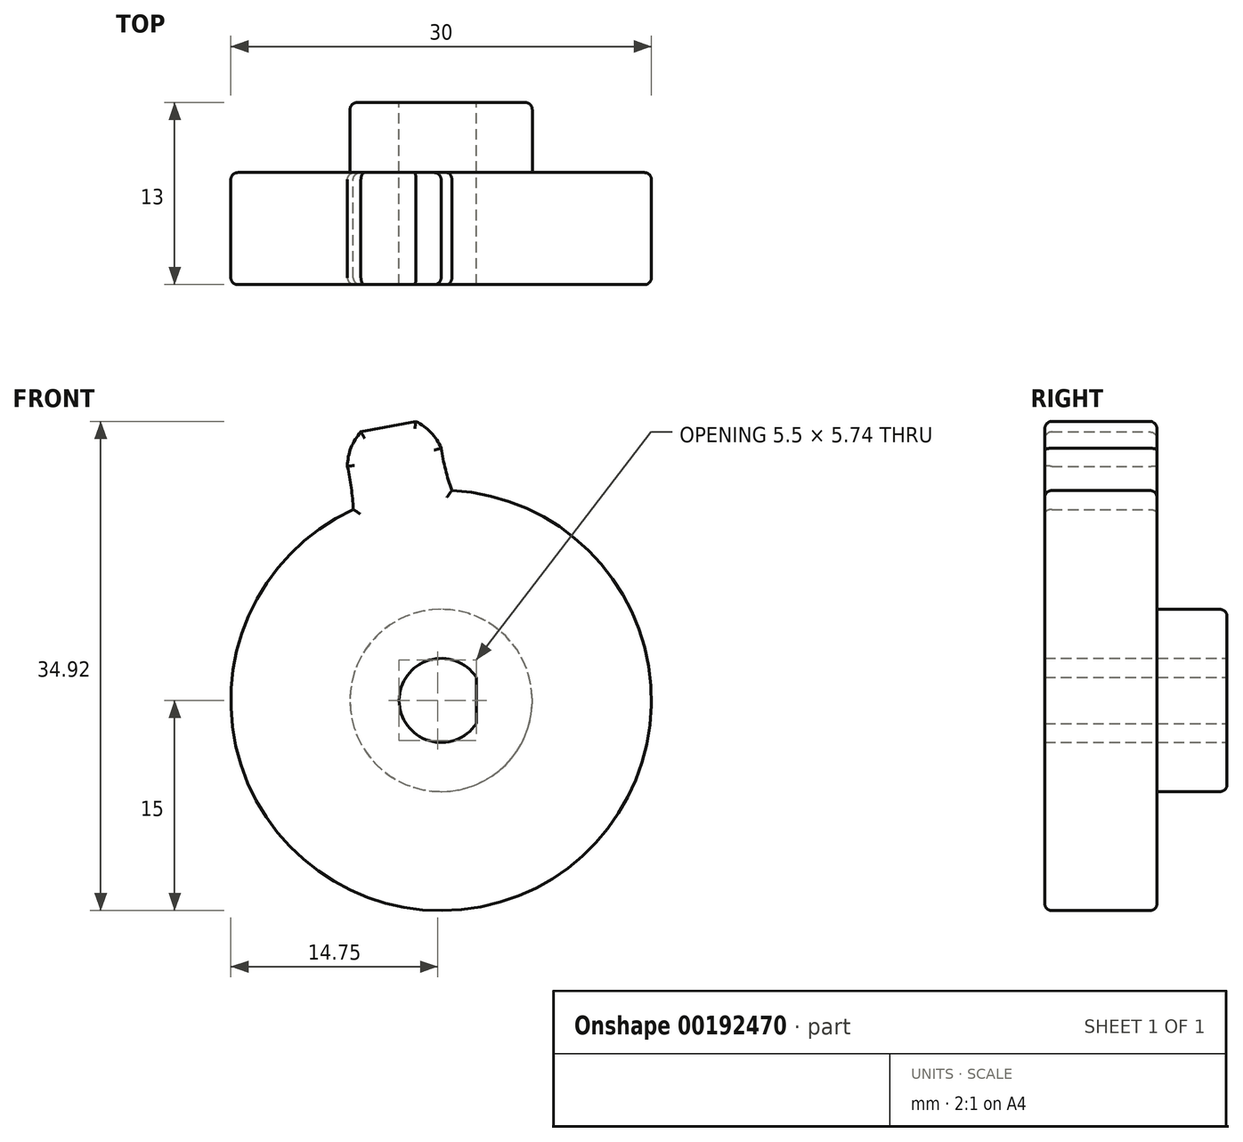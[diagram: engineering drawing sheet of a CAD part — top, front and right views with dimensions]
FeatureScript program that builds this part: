
annotation { "Feature Type Name" : "Feature", "Feature Type Description" : "" }
export const myFeature = defineFeature(function(context is Context, id is Id, definition is map)
    precondition{}
    {
        {
            var Q0;
            Q0=qCreatedBy(makeId("Front.planeOp"),FACE);
            var sketch = newSketch(context, id + "F0", { "sketchPlane" : qUnion([Q0])});
            skCircle(sketch, "E0", {"center": v(0, 0) * mm, "radius": 18 * mm, "construction": true});
            skCircle(sketch, "E1", {"center": v(0, 0) * mm, "radius": 20 * mm, "construction": true});
            skCircle(sketch, "E2", {"center": v(0, 0) * mm, "radius": 15 * mm});
            skLineSegment(sketch, "E3", {"start": v(0, 0) * mm, "end": v(0, 26.07) * mm, "construction": true});
            skLineSegment(sketch, "E4", {"start": v(0, 0) * mm, "end": v(-5, 25.97) * mm, "construction": true});
            skLineSegment(sketch, "E5", {"start": v(0, 18) * mm, "end": v(-27.92, 18) * mm, "construction": true});
            skLineSegment(sketch, "E6", {"start": v(0, 18) * mm, "end": v(-28.83, 7.5) * mm, "construction": true});
            skCircle(sketch, "E7", {"center": v(0, 18) * mm, "radius": 3.75 * mm, "construction": true});
            skCircle(sketch, "E8", {"center": v(0, 0) * mm, "radius": 16.91 * mm, "construction": true});
            skCircle(sketch, "E9", {"center": v(-3.46, 16.56) * mm, "radius": 3.75 * mm, "construction": true});
            skArc(sketch, "E10", {"start": v(0, 18) * mm, "mid": v(-0.72, 19.12) * mm, "end": v(-1.8, 19.92) * mm});
            skArc(sketch, "E11", {"start": v(0, 18) * mm, "mid": v(0.31, 16.47) * mm, "end": v(0.76, 14.98) * mm});
            skArc(sketch, "E12.MirrorCS", {"start": v(-6.68, 16.71) * mm, "mid": v(-6.4, 15.18) * mm, "end": v(-6.27, 13.63) * mm});
            skArc(sketch, "E13.MirrorCS", {"start": v(-6.68, 16.71) * mm, "mid": v(-6.43, 18.03) * mm, "end": v(-5.72, 19.16) * mm});
            skLineSegment(sketch, "E14", {"start": v(-5.72, 19.16) * mm, "end": v(-1.8, 19.92) * mm});
            skArc(sketch, "E15.1.0", {"start": v(-14.14, 11.13) * mm, "mid": v(-14.58, 12.4) * mm, "end": v(-14.54, 13.73) * mm});
            skArc(sketch, "E15.1.1", {"start": v(-14.14, 11.13) * mm, "mid": v(-13.14, 9.94) * mm, "end": v(-12.24, 8.67) * mm});
            skArc(sketch, "E15.1.2", {"start": v(-9, 15.59) * mm, "mid": v(-7.96, 14.42) * mm, "end": v(-6.83, 13.35) * mm});
            skArc(sketch, "E15.1.3", {"start": v(-9, 15.59) * mm, "mid": v(-10.19, 16.2) * mm, "end": v(-11.52, 16.35) * mm});
            skLineSegment(sketch, "E15.1.4", {"start": v(-14.54, 13.73) * mm, "end": v(-11.52, 16.35) * mm});
            skArc(sketch, "E15.2.0", {"start": v(-17.82, 2.57) * mm, "mid": v(-18.83, 3.45) * mm, "end": v(-19.46, 4.62) * mm});
            skArc(sketch, "E15.2.1", {"start": v(-17.82, 2.57) * mm, "mid": v(-16.35, 2.04) * mm, "end": v(-14.94, 1.38) * mm});
            skArc(sketch, "E15.2.2", {"start": v(-15.59, 9) * mm, "mid": v(-14.1, 8.5) * mm, "end": v(-12.6, 8.15) * mm});
            skArc(sketch, "E15.2.3", {"start": v(-15.59, 9) * mm, "mid": v(-16.92, 8.94) * mm, "end": v(-18.15, 8.4) * mm});
            skLineSegment(sketch, "E15.2.4", {"start": v(-19.46, 4.62) * mm, "end": v(-18.15, 8.4) * mm});
            skArc(sketch, "E15.3.0", {"start": v(-16.71, -6.68) * mm, "mid": v(-18.03, -6.43) * mm, "end": v(-19.16, -5.72) * mm});
            skArc(sketch, "E15.3.1", {"start": v(-16.71, -6.68) * mm, "mid": v(-15.18, -6.4) * mm, "end": v(-13.63, -6.27) * mm});
            skArc(sketch, "E15.3.2", {"start": v(-18, 0) * mm, "mid": v(-16.47, 0.31) * mm, "end": v(-14.98, 0.76) * mm});
            skArc(sketch, "E15.3.3", {"start": v(-18, 0) * mm, "mid": v(-19.12, -0.72) * mm, "end": v(-19.92, -1.8) * mm});
            skLineSegment(sketch, "E15.3.4", {"start": v(-19.16, -5.72) * mm, "end": v(-19.92, -1.8) * mm});
            skArc(sketch, "E15.4.0", {"start": v(-11.13, -14.14) * mm, "mid": v(-12.4, -14.58) * mm, "end": v(-13.73, -14.54) * mm});
            skArc(sketch, "E15.4.1", {"start": v(-11.13, -14.14) * mm, "mid": v(-9.94, -13.14) * mm, "end": v(-8.67, -12.24) * mm});
            skArc(sketch, "E15.4.2", {"start": v(-15.59, -9) * mm, "mid": v(-14.42, -7.96) * mm, "end": v(-13.35, -6.83) * mm});
            skArc(sketch, "E15.4.3", {"start": v(-15.59, -9) * mm, "mid": v(-16.2, -10.19) * mm, "end": v(-16.35, -11.52) * mm});
            skLineSegment(sketch, "E15.4.4", {"start": v(-13.73, -14.54) * mm, "end": v(-16.35, -11.52) * mm});
            skArc(sketch, "E15.5.0", {"start": v(-2.57, -17.82) * mm, "mid": v(-3.45, -18.83) * mm, "end": v(-4.62, -19.46) * mm});
            skArc(sketch, "E15.5.1", {"start": v(-2.57, -17.82) * mm, "mid": v(-2.04, -16.35) * mm, "end": v(-1.38, -14.94) * mm});
            skArc(sketch, "E15.5.2", {"start": v(-9, -15.59) * mm, "mid": v(-8.5, -14.1) * mm, "end": v(-8.15, -12.6) * mm});
            skArc(sketch, "E15.5.3", {"start": v(-9, -15.59) * mm, "mid": v(-8.94, -16.92) * mm, "end": v(-8.4, -18.15) * mm});
            skLineSegment(sketch, "E15.5.4", {"start": v(-4.62, -19.46) * mm, "end": v(-8.4, -18.15) * mm});
            skArc(sketch, "E15.6.0", {"start": v(6.68, -16.71) * mm, "mid": v(6.43, -18.03) * mm, "end": v(5.72, -19.16) * mm});
            skArc(sketch, "E15.6.1", {"start": v(6.68, -16.71) * mm, "mid": v(6.4, -15.18) * mm, "end": v(6.27, -13.63) * mm});
            skArc(sketch, "E15.6.2", {"start": v(0, -18) * mm, "mid": v(-0.31, -16.47) * mm, "end": v(-0.76, -14.98) * mm});
            skArc(sketch, "E15.6.3", {"start": v(0, -18) * mm, "mid": v(0.72, -19.12) * mm, "end": v(1.8, -19.92) * mm});
            skLineSegment(sketch, "E15.6.4", {"start": v(5.72, -19.16) * mm, "end": v(1.8, -19.92) * mm});
            skArc(sketch, "E15.7.0", {"start": v(14.14, -11.13) * mm, "mid": v(14.58, -12.4) * mm, "end": v(14.54, -13.73) * mm});
            skArc(sketch, "E15.7.1", {"start": v(14.14, -11.13) * mm, "mid": v(13.14, -9.94) * mm, "end": v(12.24, -8.67) * mm});
            skArc(sketch, "E15.7.2", {"start": v(9, -15.59) * mm, "mid": v(7.96, -14.42) * mm, "end": v(6.83, -13.35) * mm});
            skArc(sketch, "E15.7.3", {"start": v(9, -15.59) * mm, "mid": v(10.19, -16.2) * mm, "end": v(11.52, -16.35) * mm});
            skLineSegment(sketch, "E15.7.4", {"start": v(14.54, -13.73) * mm, "end": v(11.52, -16.35) * mm});
            skArc(sketch, "E15.8.0", {"start": v(17.82, -2.57) * mm, "mid": v(18.83, -3.45) * mm, "end": v(19.46, -4.62) * mm});
            skArc(sketch, "E15.8.1", {"start": v(17.82, -2.57) * mm, "mid": v(16.35, -2.04) * mm, "end": v(14.94, -1.38) * mm});
            skArc(sketch, "E15.8.2", {"start": v(15.59, -9) * mm, "mid": v(14.1, -8.5) * mm, "end": v(12.6, -8.15) * mm});
            skArc(sketch, "E15.8.3", {"start": v(15.59, -9) * mm, "mid": v(16.92, -8.94) * mm, "end": v(18.15, -8.4) * mm});
            skLineSegment(sketch, "E15.8.4", {"start": v(19.46, -4.62) * mm, "end": v(18.15, -8.4) * mm});
            skArc(sketch, "E15.9.0", {"start": v(16.71, 6.68) * mm, "mid": v(18.03, 6.43) * mm, "end": v(19.16, 5.72) * mm});
            skArc(sketch, "E15.9.1", {"start": v(16.71, 6.68) * mm, "mid": v(15.18, 6.4) * mm, "end": v(13.63, 6.27) * mm});
            skArc(sketch, "E15.9.2", {"start": v(18, 0) * mm, "mid": v(16.47, -0.31) * mm, "end": v(14.98, -0.76) * mm});
            skArc(sketch, "E15.9.3", {"start": v(18, 0) * mm, "mid": v(19.13, 0.72) * mm, "end": v(19.92, 1.8) * mm});
            skLineSegment(sketch, "E15.9.4", {"start": v(19.16, 5.72) * mm, "end": v(19.92, 1.8) * mm});
            skArc(sketch, "E15.10.0", {"start": v(11.13, 14.14) * mm, "mid": v(12.4, 14.58) * mm, "end": v(13.73, 14.54) * mm});
            skArc(sketch, "E15.10.1", {"start": v(11.13, 14.14) * mm, "mid": v(9.94, 13.14) * mm, "end": v(8.67, 12.24) * mm});
            skArc(sketch, "E15.10.2", {"start": v(15.59, 9) * mm, "mid": v(14.42, 7.96) * mm, "end": v(13.36, 6.83) * mm});
            skArc(sketch, "E15.10.3", {"start": v(15.59, 9) * mm, "mid": v(16.2, 10.19) * mm, "end": v(16.35, 11.52) * mm});
            skLineSegment(sketch, "E15.10.4", {"start": v(13.73, 14.54) * mm, "end": v(16.35, 11.52) * mm});
            skArc(sketch, "E15.11.0", {"start": v(2.57, 17.82) * mm, "mid": v(3.45, 18.83) * mm, "end": v(4.62, 19.46) * mm});
            skArc(sketch, "E15.11.1", {"start": v(2.57, 17.82) * mm, "mid": v(2.04, 16.35) * mm, "end": v(1.38, 14.94) * mm});
            skArc(sketch, "E15.11.2", {"start": v(9, 15.59) * mm, "mid": v(8.5, 14.1) * mm, "end": v(8.15, 12.6) * mm});
            skArc(sketch, "E15.11.3", {"start": v(9, 15.59) * mm, "mid": v(8.94, 16.92) * mm, "end": v(8.4, 18.15) * mm});
            skLineSegment(sketch, "E15.11.4", {"start": v(4.62, 19.46) * mm, "end": v(8.4, 18.15) * mm});
            skSolve(sketch);
        }
        {
            var Q0;
            {var subQ0=sQuery(id+"F0.wireOp",EDGE,"E2");var subQ15=makeQuery(id+"F0.imprint","INTERSECT",VERTEX,{"derivedFrom":[subQ0,sQuery(id+"F0.wireOp",EDGE,"E15.9.1")]});Q0=makeQuery(id+"F0.imprint","IMPRINT",FACE,{"disambiguationData":[TD([[makeQuery(id+"F0.imprint","IMPRINT",EDGE,{"disambiguationData":[TD([[subQ15,-1.0]])],"derivedFrom":subQ0}),1.0]])]});}
            var Q1;
            Q1=makeQuery(id+"F0.imprint","IMPRINT",FACE,{"disambiguationData":[TD([[makeQuery(id+"F0.imprint","IMPRINT",EDGE,{"derivedFrom":sQuery(id+"F0.wireOp",EDGE,"E15.2.0")}),-1.0]])]});
            var Q2;
            Q2=makeQuery(id+"F0.imprint","IMPRINT",FACE,{"disambiguationData":[TD([[makeQuery(id+"F0.imprint","IMPRINT",EDGE,{"derivedFrom":sQuery(id+"F0.wireOp",EDGE,"E15.3.0")}),-1.0]])]});
            var Q3;
            Q3=makeQuery(id+"F0.imprint","IMPRINT",FACE,{"disambiguationData":[TD([[makeQuery(id+"F0.imprint","IMPRINT",EDGE,{"derivedFrom":sQuery(id+"F0.wireOp",EDGE,"E15.4.0")}),-1.0]])]});
            var Q4;
            Q4=makeQuery(id+"F0.imprint","IMPRINT",FACE,{"disambiguationData":[TD([[makeQuery(id+"F0.imprint","IMPRINT",EDGE,{"derivedFrom":sQuery(id+"F0.wireOp",EDGE,"E15.5.0")}),-1.0]])]});
            var Q5;
            Q5=makeQuery(id+"F0.imprint","IMPRINT",FACE,{"disambiguationData":[TD([[makeQuery(id+"F0.imprint","IMPRINT",EDGE,{"derivedFrom":sQuery(id+"F0.wireOp",EDGE,"E15.6.0")}),-1.0]])]});
            var Q6;
            Q6=makeQuery(id+"F0.imprint","IMPRINT",FACE,{"disambiguationData":[TD([[makeQuery(id+"F0.imprint","IMPRINT",EDGE,{"derivedFrom":sQuery(id+"F0.wireOp",EDGE,"E15.7.0")}),-1.0]])]});
            var Q7;
            Q7=makeQuery(id+"F0.imprint","IMPRINT",FACE,{"disambiguationData":[TD([[makeQuery(id+"F0.imprint","IMPRINT",EDGE,{"derivedFrom":sQuery(id+"F0.wireOp",EDGE,"E15.8.0")}),-1.0]])]});
            var Q8;
            Q8=makeQuery(id+"F0.imprint","IMPRINT",FACE,{"disambiguationData":[TD([[makeQuery(id+"F0.imprint","IMPRINT",EDGE,{"derivedFrom":sQuery(id+"F0.wireOp",EDGE,"E15.9.0")}),-1.0]])]});
            var Q9;
            Q9=makeQuery(id+"F0.imprint","IMPRINT",FACE,{"disambiguationData":[TD([[makeQuery(id+"F0.imprint","IMPRINT",EDGE,{"derivedFrom":sQuery(id+"F0.wireOp",EDGE,"E15.10.0")}),-1.0]])]});
            var Q10;
            Q10=makeQuery(id+"F0.imprint","IMPRINT",FACE,{"disambiguationData":[TD([[makeQuery(id+"F0.imprint","IMPRINT",EDGE,{"derivedFrom":sQuery(id+"F0.wireOp",EDGE,"E15.11.0")}),-1.0]])]});
            var Q11;
            Q11=makeQuery(id+"F0.imprint","IMPRINT",FACE,{"disambiguationData":[TD([[makeQuery(id+"F0.imprint","IMPRINT",EDGE,{"derivedFrom":sQuery(id+"F0.wireOp",EDGE,"E10")}),1.0]])]});
            var Q12;
            Q12=makeQuery(id+"F0.imprint","IMPRINT",FACE,{"disambiguationData":[TD([[makeQuery(id+"F0.imprint","IMPRINT",EDGE,{"derivedFrom":sQuery(id+"F0.wireOp",EDGE,"E15.1.0")}),-1.0]])]});
            extrude(context, id + "F1", {"entities" : qUnion([Q0, Q1, Q2, Q3, Q4, Q5, Q6, Q7, Q8, Q9, Q10, Q11, Q12]), "depth" : 8 * mm});
        }
        {
            var Q0;
            Q0=makeQuery(id+"F1.opExtrude","CAP_EDGE",EDGE,{"disambiguationData":[OSD([sQuery(id+"F0.wireOp",EDGE,"E15.1.3")])],"isStart":false});
            var Q1;
            Q1=makeQuery(id+"F1.opExtrude","CAP_FACE",FACE,{"disambiguationData":[OSD([sQuery(id+"F0.wireOp",EDGE,"E2"),sQuery(id+"F0.wireOp",EDGE,"E10"),sQuery(id+"F0.wireOp",EDGE,"E11"),sQuery(id+"F0.wireOp",EDGE,"E12.MirrorCS"),sQuery(id+"F0.wireOp",EDGE,"E13.MirrorCS"),sQuery(id+"F0.wireOp",EDGE,"E14"),sQuery(id+"F0.wireOp",EDGE,"E15.1.0"),sQuery(id+"F0.wireOp",EDGE,"E15.1.1"),sQuery(id+"F0.wireOp",EDGE,"E15.1.2"),sQuery(id+"F0.wireOp",EDGE,"E15.1.3"),sQuery(id+"F0.wireOp",EDGE,"E15.1.4"),sQuery(id+"F0.wireOp",EDGE,"E15.2.0"),sQuery(id+"F0.wireOp",EDGE,"E15.2.1"),sQuery(id+"F0.wireOp",EDGE,"E15.2.2"),sQuery(id+"F0.wireOp",EDGE,"E15.2.3"),sQuery(id+"F0.wireOp",EDGE,"E15.2.4"),sQuery(id+"F0.wireOp",EDGE,"E15.3.0"),sQuery(id+"F0.wireOp",EDGE,"E15.3.1"),sQuery(id+"F0.wireOp",EDGE,"E15.3.2"),sQuery(id+"F0.wireOp",EDGE,"E15.3.3"),sQuery(id+"F0.wireOp",EDGE,"E15.3.4"),sQuery(id+"F0.wireOp",EDGE,"E15.4.0"),sQuery(id+"F0.wireOp",EDGE,"E15.4.1"),sQuery(id+"F0.wireOp",EDGE,"E15.4.2"),sQuery(id+"F0.wireOp",EDGE,"E15.4.3"),sQuery(id+"F0.wireOp",EDGE,"E15.4.4"),sQuery(id+"F0.wireOp",EDGE,"E15.5.0"),sQuery(id+"F0.wireOp",EDGE,"E15.5.1"),sQuery(id+"F0.wireOp",EDGE,"E15.5.2"),sQuery(id+"F0.wireOp",EDGE,"E15.5.3"),sQuery(id+"F0.wireOp",EDGE,"E15.5.4"),sQuery(id+"F0.wireOp",EDGE,"E15.6.0"),sQuery(id+"F0.wireOp",EDGE,"E15.6.1"),sQuery(id+"F0.wireOp",EDGE,"E15.6.2"),sQuery(id+"F0.wireOp",EDGE,"E15.6.3"),sQuery(id+"F0.wireOp",EDGE,"E15.6.4"),sQuery(id+"F0.wireOp",EDGE,"E15.7.0"),sQuery(id+"F0.wireOp",EDGE,"E15.7.1"),sQuery(id+"F0.wireOp",EDGE,"E15.7.2"),sQuery(id+"F0.wireOp",EDGE,"E15.7.3"),sQuery(id+"F0.wireOp",EDGE,"E15.7.4"),sQuery(id+"F0.wireOp",EDGE,"E15.8.0"),sQuery(id+"F0.wireOp",EDGE,"E15.8.1"),sQuery(id+"F0.wireOp",EDGE,"E15.8.2"),sQuery(id+"F0.wireOp",EDGE,"E15.8.3"),sQuery(id+"F0.wireOp",EDGE,"E15.8.4"),sQuery(id+"F0.wireOp",EDGE,"E15.9.0"),sQuery(id+"F0.wireOp",EDGE,"E15.9.1"),sQuery(id+"F0.wireOp",EDGE,"E15.9.2"),sQuery(id+"F0.wireOp",EDGE,"E15.9.3"),sQuery(id+"F0.wireOp",EDGE,"E15.9.4"),sQuery(id+"F0.wireOp",EDGE,"E15.10.0"),sQuery(id+"F0.wireOp",EDGE,"E15.10.1"),sQuery(id+"F0.wireOp",EDGE,"E15.10.2"),sQuery(id+"F0.wireOp",EDGE,"E15.10.3"),sQuery(id+"F0.wireOp",EDGE,"E15.10.4"),sQuery(id+"F0.wireOp",EDGE,"E15.11.0"),sQuery(id+"F0.wireOp",EDGE,"E15.11.1"),sQuery(id+"F0.wireOp",EDGE,"E15.11.2"),sQuery(id+"F0.wireOp",EDGE,"E15.11.3"),sQuery(id+"F0.wireOp",EDGE,"E15.11.4")])],"isStart":false});
            var Q2;
            Q2=makeQuery(id+"F1.opExtrude","CAP_FACE",FACE,{"disambiguationData":[OSD([sQuery(id+"F0.wireOp",EDGE,"E2"),sQuery(id+"F0.wireOp",EDGE,"E10"),sQuery(id+"F0.wireOp",EDGE,"E11"),sQuery(id+"F0.wireOp",EDGE,"E12.MirrorCS"),sQuery(id+"F0.wireOp",EDGE,"E13.MirrorCS"),sQuery(id+"F0.wireOp",EDGE,"E14"),sQuery(id+"F0.wireOp",EDGE,"E15.1.0"),sQuery(id+"F0.wireOp",EDGE,"E15.1.1"),sQuery(id+"F0.wireOp",EDGE,"E15.1.2"),sQuery(id+"F0.wireOp",EDGE,"E15.1.3"),sQuery(id+"F0.wireOp",EDGE,"E15.1.4"),sQuery(id+"F0.wireOp",EDGE,"E15.2.0"),sQuery(id+"F0.wireOp",EDGE,"E15.2.1"),sQuery(id+"F0.wireOp",EDGE,"E15.2.2"),sQuery(id+"F0.wireOp",EDGE,"E15.2.3"),sQuery(id+"F0.wireOp",EDGE,"E15.2.4"),sQuery(id+"F0.wireOp",EDGE,"E15.3.0"),sQuery(id+"F0.wireOp",EDGE,"E15.3.1"),sQuery(id+"F0.wireOp",EDGE,"E15.3.2"),sQuery(id+"F0.wireOp",EDGE,"E15.3.3"),sQuery(id+"F0.wireOp",EDGE,"E15.3.4"),sQuery(id+"F0.wireOp",EDGE,"E15.4.0"),sQuery(id+"F0.wireOp",EDGE,"E15.4.1"),sQuery(id+"F0.wireOp",EDGE,"E15.4.2"),sQuery(id+"F0.wireOp",EDGE,"E15.4.3"),sQuery(id+"F0.wireOp",EDGE,"E15.4.4"),sQuery(id+"F0.wireOp",EDGE,"E15.5.0"),sQuery(id+"F0.wireOp",EDGE,"E15.5.1"),sQuery(id+"F0.wireOp",EDGE,"E15.5.2"),sQuery(id+"F0.wireOp",EDGE,"E15.5.3"),sQuery(id+"F0.wireOp",EDGE,"E15.5.4"),sQuery(id+"F0.wireOp",EDGE,"E15.6.0"),sQuery(id+"F0.wireOp",EDGE,"E15.6.1"),sQuery(id+"F0.wireOp",EDGE,"E15.6.2"),sQuery(id+"F0.wireOp",EDGE,"E15.6.3"),sQuery(id+"F0.wireOp",EDGE,"E15.6.4"),sQuery(id+"F0.wireOp",EDGE,"E15.7.0"),sQuery(id+"F0.wireOp",EDGE,"E15.7.1"),sQuery(id+"F0.wireOp",EDGE,"E15.7.2"),sQuery(id+"F0.wireOp",EDGE,"E15.7.3"),sQuery(id+"F0.wireOp",EDGE,"E15.7.4"),sQuery(id+"F0.wireOp",EDGE,"E15.8.0"),sQuery(id+"F0.wireOp",EDGE,"E15.8.1"),sQuery(id+"F0.wireOp",EDGE,"E15.8.2"),sQuery(id+"F0.wireOp",EDGE,"E15.8.3"),sQuery(id+"F0.wireOp",EDGE,"E15.8.4"),sQuery(id+"F0.wireOp",EDGE,"E15.9.0"),sQuery(id+"F0.wireOp",EDGE,"E15.9.1"),sQuery(id+"F0.wireOp",EDGE,"E15.9.2"),sQuery(id+"F0.wireOp",EDGE,"E15.9.3"),sQuery(id+"F0.wireOp",EDGE,"E15.9.4"),sQuery(id+"F0.wireOp",EDGE,"E15.10.0"),sQuery(id+"F0.wireOp",EDGE,"E15.10.1"),sQuery(id+"F0.wireOp",EDGE,"E15.10.2"),sQuery(id+"F0.wireOp",EDGE,"E15.10.3"),sQuery(id+"F0.wireOp",EDGE,"E15.10.4"),sQuery(id+"F0.wireOp",EDGE,"E15.11.0"),sQuery(id+"F0.wireOp",EDGE,"E15.11.1"),sQuery(id+"F0.wireOp",EDGE,"E15.11.2"),sQuery(id+"F0.wireOp",EDGE,"E15.11.3"),sQuery(id+"F0.wireOp",EDGE,"E15.11.4")])],"isStart":true});
            fillet(context, id + "F2", {"entities" : qUnion([Q0, Q1, Q2]), "radius" : 0.5 * mm, "tangentPropagation" : true, "allowEdgeOverflow" : false});
        }
        {
            var Q0;
            Q0=makeQuery(id+"F1.opExtrude","CAP_FACE",FACE,{"disambiguationData":[OSD([sQuery(id+"F0.wireOp",EDGE,"E2"),sQuery(id+"F0.wireOp",EDGE,"E10"),sQuery(id+"F0.wireOp",EDGE,"E11"),sQuery(id+"F0.wireOp",EDGE,"E12.MirrorCS"),sQuery(id+"F0.wireOp",EDGE,"E13.MirrorCS"),sQuery(id+"F0.wireOp",EDGE,"E14"),sQuery(id+"F0.wireOp",EDGE,"E15.1.0"),sQuery(id+"F0.wireOp",EDGE,"E15.1.1"),sQuery(id+"F0.wireOp",EDGE,"E15.1.2"),sQuery(id+"F0.wireOp",EDGE,"E15.1.3"),sQuery(id+"F0.wireOp",EDGE,"E15.1.4"),sQuery(id+"F0.wireOp",EDGE,"E15.2.0"),sQuery(id+"F0.wireOp",EDGE,"E15.2.1"),sQuery(id+"F0.wireOp",EDGE,"E15.2.2"),sQuery(id+"F0.wireOp",EDGE,"E15.2.3"),sQuery(id+"F0.wireOp",EDGE,"E15.2.4"),sQuery(id+"F0.wireOp",EDGE,"E15.3.0"),sQuery(id+"F0.wireOp",EDGE,"E15.3.1"),sQuery(id+"F0.wireOp",EDGE,"E15.3.2"),sQuery(id+"F0.wireOp",EDGE,"E15.3.3"),sQuery(id+"F0.wireOp",EDGE,"E15.3.4"),sQuery(id+"F0.wireOp",EDGE,"E15.4.0"),sQuery(id+"F0.wireOp",EDGE,"E15.4.1"),sQuery(id+"F0.wireOp",EDGE,"E15.4.2"),sQuery(id+"F0.wireOp",EDGE,"E15.4.3"),sQuery(id+"F0.wireOp",EDGE,"E15.4.4"),sQuery(id+"F0.wireOp",EDGE,"E15.5.0"),sQuery(id+"F0.wireOp",EDGE,"E15.5.1"),sQuery(id+"F0.wireOp",EDGE,"E15.5.2"),sQuery(id+"F0.wireOp",EDGE,"E15.5.3"),sQuery(id+"F0.wireOp",EDGE,"E15.5.4"),sQuery(id+"F0.wireOp",EDGE,"E15.6.0"),sQuery(id+"F0.wireOp",EDGE,"E15.6.1"),sQuery(id+"F0.wireOp",EDGE,"E15.6.2"),sQuery(id+"F0.wireOp",EDGE,"E15.6.3"),sQuery(id+"F0.wireOp",EDGE,"E15.6.4"),sQuery(id+"F0.wireOp",EDGE,"E15.7.0"),sQuery(id+"F0.wireOp",EDGE,"E15.7.1"),sQuery(id+"F0.wireOp",EDGE,"E15.7.2"),sQuery(id+"F0.wireOp",EDGE,"E15.7.3"),sQuery(id+"F0.wireOp",EDGE,"E15.7.4"),sQuery(id+"F0.wireOp",EDGE,"E15.8.0"),sQuery(id+"F0.wireOp",EDGE,"E15.8.1"),sQuery(id+"F0.wireOp",EDGE,"E15.8.2"),sQuery(id+"F0.wireOp",EDGE,"E15.8.3"),sQuery(id+"F0.wireOp",EDGE,"E15.8.4"),sQuery(id+"F0.wireOp",EDGE,"E15.9.0"),sQuery(id+"F0.wireOp",EDGE,"E15.9.1"),sQuery(id+"F0.wireOp",EDGE,"E15.9.2"),sQuery(id+"F0.wireOp",EDGE,"E15.9.3"),sQuery(id+"F0.wireOp",EDGE,"E15.9.4"),sQuery(id+"F0.wireOp",EDGE,"E15.10.0"),sQuery(id+"F0.wireOp",EDGE,"E15.10.1"),sQuery(id+"F0.wireOp",EDGE,"E15.10.2"),sQuery(id+"F0.wireOp",EDGE,"E15.10.3"),sQuery(id+"F0.wireOp",EDGE,"E15.10.4"),sQuery(id+"F0.wireOp",EDGE,"E15.11.0"),sQuery(id+"F0.wireOp",EDGE,"E15.11.1"),sQuery(id+"F0.wireOp",EDGE,"E15.11.2"),sQuery(id+"F0.wireOp",EDGE,"E15.11.3"),sQuery(id+"F0.wireOp",EDGE,"E15.11.4")])],"isStart":true});
            var sketch = newSketch(context, id + "F3", { "sketchPlane" : qUnion([Q0])});
            skCircle(sketch, "E16", {"center": v(0, 0) * mm, "radius": 3 * mm});
            skLineSegment(sketch, "E17", {"start": v(-2.5, -1.66) * mm, "end": v(-2.5, 1.66) * mm});
            skSolve(sketch);
        }
        {
            var Q0;
            {var subQ0=sQuery(id+"F3.wireOp",EDGE,"E17");Q0=makeQuery(id+"F3.imprint","IMPRINT",FACE,{"disambiguationData":[TD([[makeQuery(id+"F3.imprint","IMPRINT",EDGE,{"derivedFrom":subQ0}),-1.0]])]});}
            extrude(context, id + "F4", {"entities" : qUnion([Q0]), "operationType" : NewBodyOperationType.REMOVE, "endBound" : BoundingType.THROUGH_ALL, "oppositeDirection" : true, "depth" : 25 * mm});
        }
        {
            var Q0;
            Q0=makeQuery(id+"F1.opExtrude","CAP_FACE",FACE,{"disambiguationData":[OSD([sQuery(id+"F0.wireOp",EDGE,"E2"),sQuery(id+"F0.wireOp",EDGE,"E10"),sQuery(id+"F0.wireOp",EDGE,"E11"),sQuery(id+"F0.wireOp",EDGE,"E12.MirrorCS"),sQuery(id+"F0.wireOp",EDGE,"E13.MirrorCS"),sQuery(id+"F0.wireOp",EDGE,"E14"),sQuery(id+"F0.wireOp",EDGE,"E15.1.0"),sQuery(id+"F0.wireOp",EDGE,"E15.1.1"),sQuery(id+"F0.wireOp",EDGE,"E15.1.2"),sQuery(id+"F0.wireOp",EDGE,"E15.1.3"),sQuery(id+"F0.wireOp",EDGE,"E15.1.4"),sQuery(id+"F0.wireOp",EDGE,"E15.2.0"),sQuery(id+"F0.wireOp",EDGE,"E15.2.1"),sQuery(id+"F0.wireOp",EDGE,"E15.2.2"),sQuery(id+"F0.wireOp",EDGE,"E15.2.3"),sQuery(id+"F0.wireOp",EDGE,"E15.2.4"),sQuery(id+"F0.wireOp",EDGE,"E15.3.0"),sQuery(id+"F0.wireOp",EDGE,"E15.3.1"),sQuery(id+"F0.wireOp",EDGE,"E15.3.2"),sQuery(id+"F0.wireOp",EDGE,"E15.3.3"),sQuery(id+"F0.wireOp",EDGE,"E15.3.4"),sQuery(id+"F0.wireOp",EDGE,"E15.4.0"),sQuery(id+"F0.wireOp",EDGE,"E15.4.1"),sQuery(id+"F0.wireOp",EDGE,"E15.4.2"),sQuery(id+"F0.wireOp",EDGE,"E15.4.3"),sQuery(id+"F0.wireOp",EDGE,"E15.4.4"),sQuery(id+"F0.wireOp",EDGE,"E15.5.0"),sQuery(id+"F0.wireOp",EDGE,"E15.5.1"),sQuery(id+"F0.wireOp",EDGE,"E15.5.2"),sQuery(id+"F0.wireOp",EDGE,"E15.5.3"),sQuery(id+"F0.wireOp",EDGE,"E15.5.4"),sQuery(id+"F0.wireOp",EDGE,"E15.6.0"),sQuery(id+"F0.wireOp",EDGE,"E15.6.1"),sQuery(id+"F0.wireOp",EDGE,"E15.6.2"),sQuery(id+"F0.wireOp",EDGE,"E15.6.3"),sQuery(id+"F0.wireOp",EDGE,"E15.6.4"),sQuery(id+"F0.wireOp",EDGE,"E15.7.0"),sQuery(id+"F0.wireOp",EDGE,"E15.7.1"),sQuery(id+"F0.wireOp",EDGE,"E15.7.2"),sQuery(id+"F0.wireOp",EDGE,"E15.7.3"),sQuery(id+"F0.wireOp",EDGE,"E15.7.4"),sQuery(id+"F0.wireOp",EDGE,"E15.8.0"),sQuery(id+"F0.wireOp",EDGE,"E15.8.1"),sQuery(id+"F0.wireOp",EDGE,"E15.8.2"),sQuery(id+"F0.wireOp",EDGE,"E15.8.3"),sQuery(id+"F0.wireOp",EDGE,"E15.8.4"),sQuery(id+"F0.wireOp",EDGE,"E15.9.0"),sQuery(id+"F0.wireOp",EDGE,"E15.9.1"),sQuery(id+"F0.wireOp",EDGE,"E15.9.2"),sQuery(id+"F0.wireOp",EDGE,"E15.9.3"),sQuery(id+"F0.wireOp",EDGE,"E15.9.4"),sQuery(id+"F0.wireOp",EDGE,"E15.10.0"),sQuery(id+"F0.wireOp",EDGE,"E15.10.1"),sQuery(id+"F0.wireOp",EDGE,"E15.10.2"),sQuery(id+"F0.wireOp",EDGE,"E15.10.3"),sQuery(id+"F0.wireOp",EDGE,"E15.10.4"),sQuery(id+"F0.wireOp",EDGE,"E15.11.0"),sQuery(id+"F0.wireOp",EDGE,"E15.11.1"),sQuery(id+"F0.wireOp",EDGE,"E15.11.2"),sQuery(id+"F0.wireOp",EDGE,"E15.11.3"),sQuery(id+"F0.wireOp",EDGE,"E15.11.4")])],"isStart":true});
            var sketch = newSketch(context, id + "F5", { "sketchPlane" : qUnion([Q0])});
            skCircle(sketch, "E18", {"center": v(0, 0) * mm, "radius": 6.5 * mm});
            skSolve(sketch);
        }
        {
            var Q0;
            Q0=makeQuery(id+"F5.imprint","IMPRINT",FACE,{"disambiguationData":[TD([[makeQuery(id+"F5.imprint","IMPRINT",EDGE,{"derivedFrom":sQuery(id+"F5.wireOp",EDGE,"E18")}),1.0]])]});
            extrude(context, id + "F6", {"entities" : qUnion([Q0]), "operationType" : NewBodyOperationType.ADD, "depth" : 5 * mm});
        }
        {
            var Q0;
            Q0=makeQuery(id+"F6.opExtrude","CAP_EDGE",EDGE,{"disambiguationData":[OSD([sQuery(id+"F5.wireOp",EDGE,"E18")])],"isStart":true});
            var Q1;
            Q1=makeQuery(id+"F6.opExtrude","CAP_EDGE",EDGE,{"disambiguationData":[OSD([sQuery(id+"F5.wireOp",EDGE,"E18")])],"isStart":false});
            fillet(context, id + "F7", {"entities" : qUnion([Q0, Q1]), "radius" : 0.5 * mm, "tangentPropagation" : true, "allowEdgeOverflow" : false});
        }
    });
